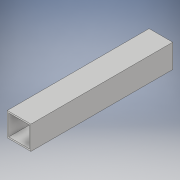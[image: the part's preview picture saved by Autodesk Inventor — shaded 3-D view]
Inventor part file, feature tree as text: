
AUTODESK INVENTOR PART (.ipt)
format: ipt  version: 2018 (Build 220112000, 112)  size: 95,232 bytes
history: native  units: in
note: dims shown in document units (in); Inventor stores cm internally (conversion verified against a paired STEP export)
features: extrude x1, sketch x1
ambient origin geometry x8: Origin, YZ Plane, XZ Plane, XY Plane, X Axis, Y Axis, Z Axis, Center Point
bodies: Solid1 (feature_tree)
feature tree (2):
  extrude  "Extrusion1"  Depth=0.875in
  sketch  "Sketch1"  dims[d0=1.0in d4=0.875in d5=6.0in d6=0.0in]
